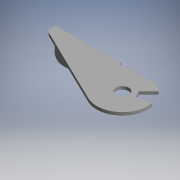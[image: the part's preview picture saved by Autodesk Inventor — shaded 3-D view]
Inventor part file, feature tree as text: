
AUTODESK INVENTOR PART (.ipt)
format: ipt  version: 2017.3 (Build 213256000, 256)  size: 159,232 bytes
history: native  units: mm (DEFAULTED — no unit token found)
features: other x21, extrude x6, sketch x6
ambient origin geometry x8: Origin, YZ Plane, XZ Plane, XY Plane, X Axis, Y Axis, Z Axis, Center Point
bodies: Solid1 (feature_tree)
feature tree (33):
  extrude  "Extrusion1"  Depth=188.0mm TaperAngle=0.0deg
  extrude  "Extrusion2"  Depth=4.0mm TaperAngle=0.0deg
  extrude  "Extrusion3"  Depth=20.0mm TaperAngle=0.0deg
  extrude  "Extrusion4"  [1 undecoded]
  extrude  "Extrusion5"  [1 undecoded]
  extrude  "Extrusion6"  [1 undecoded]
  other  "fix_end_r_XY"
  other  "fix_end_r_YZ"
  other  "fix_end_r_ZX"
  other  "fix_end_r_X"
  other  "fix_end_r_Y"
  other  "fix_end_r_Z"
  other  "fix_end_r_Center"
  other  "free_end_r_XY"
  other  "free_end_r_YZ"
  other  "free_end_r_ZX"
  other  "free_end_r_X"
  other  "free_end_r_Y"
  other  "free_end_r_Z"
  other  "free_end_r_Center"
  other  "r_XY"
  other  "r_YZ"
  other  "r_ZX"
  other  "r_X"
  other  "r_Y"
  other  "r_Z"
  other  "r_Center"
  sketch  "Sketch_10"
  sketch  "Sketch_1"  dims[d0=20.0mm d1=0.0mm d2=188.0mm d3=0.0mm]
  sketch  "Sketch_3"  dims[d8=4.0mm d9=0.0mm d10=20.0mm d11=0.0mm]
  sketch  "Sketch_2"  dims[d4=34.0mm d5=0.0mm d6=4.0mm d7=0.0mm]
  sketch  "Sketch_4"  dims[d12=0.0mm d13=0.0mm]
  sketch  "Sketch_7"
note: 3 required parameter values undecoded (feature->parameter linkage not recoverable at this tier; creation-order binding heuristic only, values carry confidence <= 0.55)
